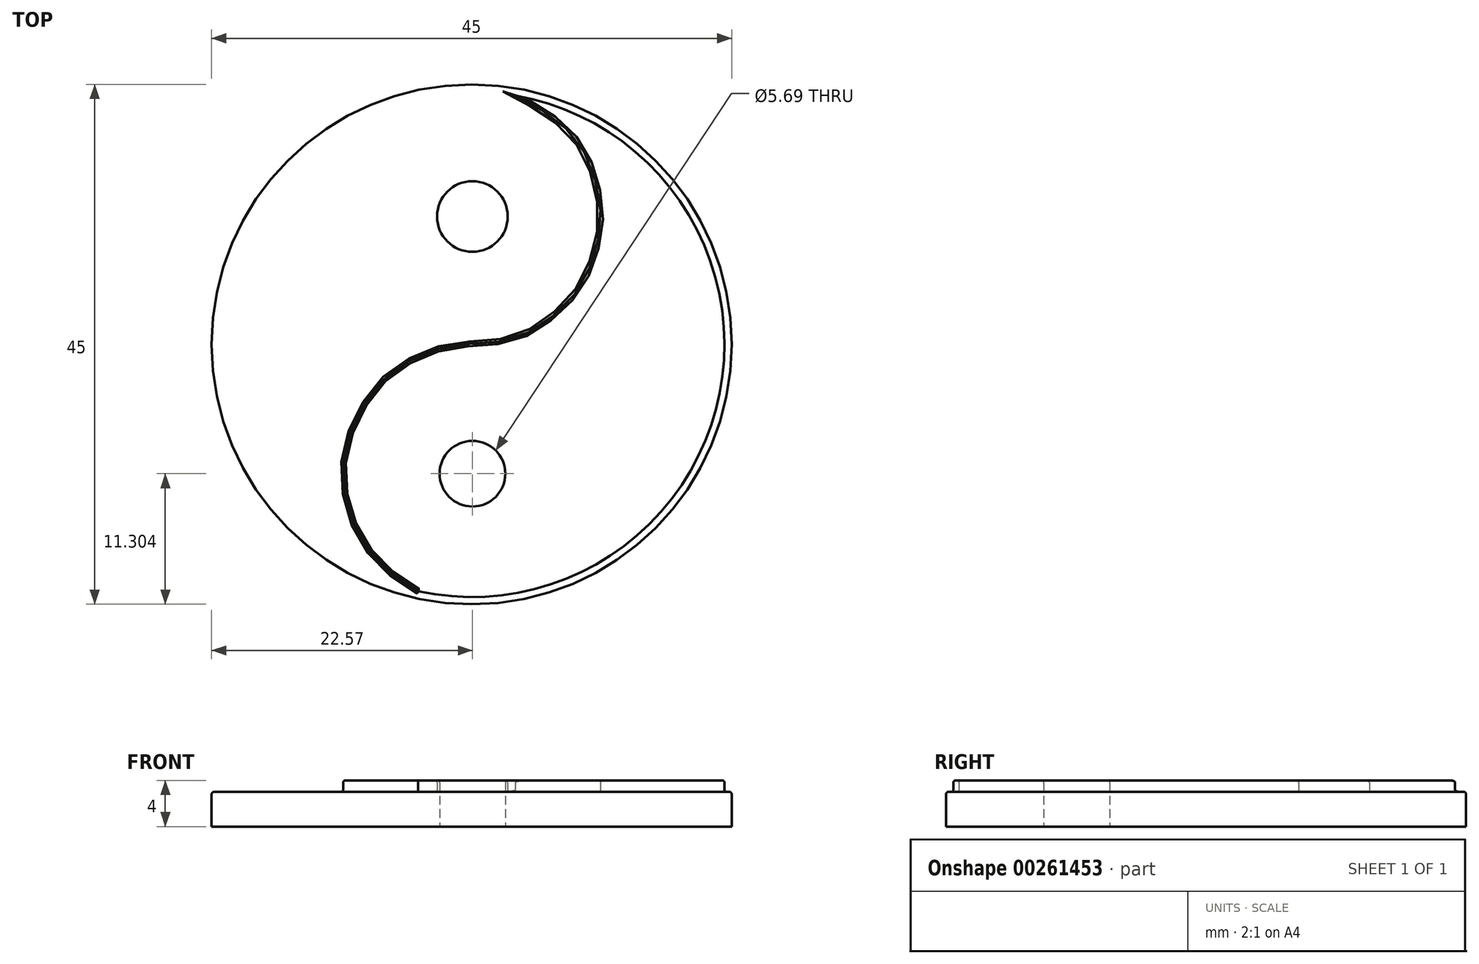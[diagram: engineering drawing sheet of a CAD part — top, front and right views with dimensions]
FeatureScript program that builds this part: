
annotation { "Feature Type Name" : "Feature", "Feature Type Description" : "" }
export const myFeature = defineFeature(function(context is Context, id is Id, definition is map)
    precondition{}
    {
        {
            var Q0;
            Q0=qCreatedBy(makeId("Top.planeOp"),FACE);
            var sketch = newSketch(context, id + "F0", { "sketchPlane" : qUnion([Q0])});
            skCircle(sketch, "E0", {"center": v(0, 0) * mm, "radius": 22.5 * mm});
            skCircle(sketch, "E1", {"center": v(0, 0) * mm, "radius": 21.88 * mm});
            skFitSpline(sketch, "E2", {"points": [v(-4.63, -21.38) * mm, v(-7.61, -19.27) * mm, v(-10.19, -15.55) * mm, v(-11.01, -9.66) * mm, v(-8.53, -4.1) * mm, v(-5.74, -1.64) * mm, v(-1.66, -0.1) * mm, v(2.92, 0.32) * mm, v(6.17, 1.81) * mm, v(8.78, 4.2) * mm, v(10.1, 6.4) * mm, v(10.97, 9.19) * mm, v(11.13, 11.72) * mm, v(10.6, 14.54) * mm, v(9.39, 17.22) * mm, v(7.24, 19.47) * mm, v(3.79, 21.54) * mm], "startDerivative": vector(-50.13, 30) * mm, "endDerivative": vector(-56.66, 30.54) * mm});
            skCircle(sketch, "E3", {"center": v(0.06, 11.07) * mm, "radius": 3.06 * mm});
            skPoint(sketch, "E3.first.point", {"position": v(0, 14.13) * mm});
            skPoint(sketch, "E3.second.point", {"position": v(0, 8.01) * mm});
            skPoint(sketch, "E3.third.point", {"position": v(3.05, 10.45) * mm});
            skCircle(sketch, "E4", {"center": v(0.07, -11.2) * mm, "radius": 2.84 * mm});
            skPoint(sketch, "E4.first.point", {"position": v(0, -8.35) * mm});
            skPoint(sketch, "E4.second.point", {"position": v(0, -14.04) * mm});
            skPoint(sketch, "E4.third.point", {"position": v(2.9, -11.02) * mm});
            skSolve(sketch);
        }
        {
            var Q0;
            Q0=makeQuery(id+"F0.imprint","IMPRINT",FACE,{"disambiguationData":[TD([[makeQuery(id+"F0.imprint","IMPRINT",EDGE,{"derivedFrom":sQuery(id+"F0.wireOp",EDGE,"E0")}),1.0]])]});
            var Q1;
            {var subQ0=sQuery(id+"F0.wireOp",EDGE,"E2");Q1=makeQuery(id+"F0.imprint","IMPRINT",FACE,{"disambiguationData":[TD([[makeQuery(id+"F0.imprint","IMPRINT",EDGE,{"derivedFrom":subQ0}),1.0]])]});}
            extrude(context, id + "F1", {"entities" : qUnion([Q0, Q1]), "depth" : 3 * mm});
        }
        {
            var Q0;
            {var subQ0=sQuery(id+"F0.wireOp",EDGE,"E2");Q0=makeQuery(id+"F0.imprint","IMPRINT",FACE,{"disambiguationData":[TD([[makeQuery(id+"F0.imprint","IMPRINT",EDGE,{"derivedFrom":subQ0}),-1.0]])]});}
            var Q1;
            Q1=makeQuery(id+"F0.imprint","IMPRINT",FACE,{"disambiguationData":[TD([[makeQuery(id+"F0.imprint","IMPRINT",EDGE,{"derivedFrom":sQuery(id+"F0.wireOp",EDGE,"E3")}),1.0]])]});
            extrude(context, id + "F2", {"entities" : qUnion([Q0, Q1]), "operationType" : NewBodyOperationType.ADD, "depth" : 4 * mm});
        }
        {
            var Q0;
            Q0=makeQuery(id+"F2.opExtrude","CAP_FACE",FACE,{"disambiguationData":[OSD([sQuery(id+"F0.wireOp",EDGE,"E3")])],"isStart":false});
            var Q1;
            Q1=makeQuery(id+"F1.opExtrude","CAP_FACE",FACE,{"disambiguationData":[OSD([sQuery(id+"F0.wireOp",EDGE,"E0"),sQuery(id+"F0.wireOp",EDGE,"E1"),sQuery(id+"F0.wireOp",EDGE,"E2"),sQuery(id+"F0.wireOp",EDGE,"E3")])],"isStart":false});
            var Q2;
            Q2=makeQuery(id+"F2.opExtrude","CAP_FACE",FACE,{"disambiguationData":[OSD([sQuery(id+"F0.wireOp",EDGE,"E1"),sQuery(id+"F0.wireOp",EDGE,"E2"),sQuery(id+"F0.wireOp",EDGE,"E4")])],"isStart":false});
            fillet(context, id + "F3", {"entities" : qUnion([Q0, Q1, Q2]), "radius" : .2 * mm, "tangentPropagation" : true, "allowEdgeOverflow" : false});
        }
    });
